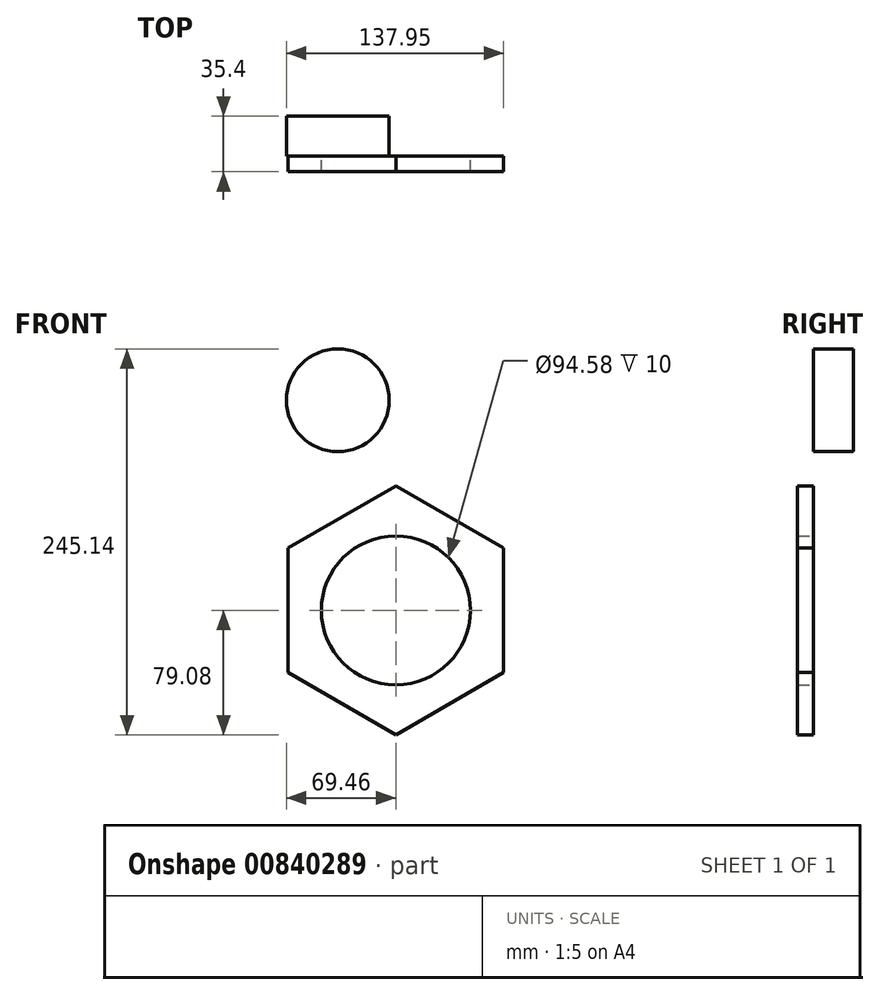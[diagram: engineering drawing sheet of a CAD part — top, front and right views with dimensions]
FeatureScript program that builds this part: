
annotation { "Feature Type Name" : "Feature", "Feature Type Description" : "" }
export const myFeature = defineFeature(function(context is Context, id is Id, definition is map)
    precondition{}
    {
        {
            var Q0;
            Q0=qCreatedBy(makeId("Front.planeOp"),FACE);
            var sketch = newSketch(context, id + "F0", { "sketchPlane" : qUnion([Q0])});
            skCircle(sketch, "E0.cCircle", {"center": v(0, 0) * mm, "radius": 79.08 * mm, "construction": true});
            skLineSegment(sketch, "E0.0", {"start": v(0, -79.08) * mm, "end": v(-68.49, -39.54) * mm});
            skLineSegment(sketch, "E0.1", {"start": v(-68.49, -39.54) * mm, "end": v(-68.49, 39.54) * mm});
            skLineSegment(sketch, "E0.2", {"start": v(-68.49, 39.54) * mm, "end": v(0, 79.08) * mm});
            skLineSegment(sketch, "E0.3", {"start": v(0, 79.08) * mm, "end": v(68.49, 39.54) * mm});
            skLineSegment(sketch, "E0.4", {"start": v(68.49, 39.54) * mm, "end": v(68.49, -39.54) * mm});
            skLineSegment(sketch, "E0.5", {"start": v(68.49, -39.54) * mm, "end": v(0, -79.08) * mm});
            skLineSegment(sketch, "E1.0", {"start": v(-2133.6, 3616.42) * mm, "end": v(-4198.71, 2424.13) * mm, "construction": true});
            skLineSegment(sketch, "E1.1", {"start": v(-4198.71, 2424.13) * mm, "end": v(-4198.71, 39.54) * mm, "construction": true});
            skCircle(sketch, "E2.0", {"center": v(0, 0) * mm, "radius": 4346.28 * mm, "construction": true});
            skSolve(sketch);
        }
        {
            var Q0;
            Q0=makeQuery(id+"F0.imprint","IMPRINT",FACE,{"disambiguationData":[TD([[makeQuery(id+"F0.imprint","IMPRINT",EDGE,{"derivedFrom":sQuery(id+"F0.wireOp",EDGE,"E0.0")}),-1.0]])]});
            var Q1;
            Q1=sQuery(id+"F0.wireOp",EDGE,"E0.0");
            var Q2;
            Q2=sQuery(id+"F0.wireOp",EDGE,"E0.2");
            var Q3;
            Q3=sQuery(id+"F0.wireOp",EDGE,"E0.4");
            var Q4;
            Q4=sQuery(id+"F0.wireOp",EDGE,"E0.3");
            var Q5;
            Q5=sQuery(id+"F0.wireOp",EDGE,"E0.1");
            extrude(context, id + "F1", {"entities" : qUnion([Q0]), "surfaceEntities" : qUnion([Q1, Q2, Q3, Q4, Q5]), "depth" : 10 * mm, "offsetDistance" : 25.4 * mm});
        }
        {
            var Q0;
            Q0=qCreatedBy(makeId("Front.planeOp"),FACE);
            var sketch = newSketch(context, id + "F2", { "sketchPlane" : qUnion([Q0])});
            skCircle(sketch, "E3", {"center": v(0, 0) * mm, "radius": 45.5 * mm});
            skSolve(sketch);
        }
        {
            var Q0;
            Q0 = qSketchRegion(id + "F2", true);
            extrude(context, id + "F3", {"entities" : qUnion([Q0]), "operationType" : NewBodyOperationType.REMOVE, "oppositeDirection" : true, "depth" : 25.4 * mm, "offsetDistance" : 25.4 * mm});
        }
        {
            var Q0;
            Q0=qCreatedBy(makeId("Front.planeOp"),FACE);
            var sketch = newSketch(context, id + "F4", { "sketchPlane" : qUnion([Q0])});
            skCircle(sketch, "E4", {"center": v(0, 0) * mm, "radius": 47.2 * mm});
            skSolve(sketch);
        }
        {
            var Q0;
            Q0 = qSketchRegion(id + "F4", true);
            extrude(context, id + "F5", {"entities" : qUnion([Q0]), "operationType" : NewBodyOperationType.REMOVE, "oppositeDirection" : true, "depth" : 25.4 * mm, "offsetDistance" : 25.4 * mm});
        }
        {
            var Q0;
            Q0=qCreatedBy(makeId("Front.planeOp"),FACE);
            var sketch = newSketch(context, id + "F6", { "sketchPlane" : qUnion([Q0])});
            skCircle(sketch, "E5", {"center": v(0, 0) * mm, "radius": 46.38 * mm});
            skSolve(sketch);
        }
        {
            var Q0;
            Q0 = qSketchRegion(id + "F6", true);
            extrude(context, id + "F7", {"entities" : qUnion([Q0]), "operationType" : NewBodyOperationType.REMOVE, "oppositeDirection" : true, "depth" : 10 * mm, "offsetDistance" : 25.4 * mm});
        }
        {
            var Q0;
            Q0=makeQuery(id+"F1.opExtrude","CAP_FACE",FACE,{"disambiguationData":[OSD([sQuery(id+"F0.wireOp",EDGE,"E0.0"),sQuery(id+"F0.wireOp",EDGE,"E0.1"),sQuery(id+"F0.wireOp",EDGE,"E0.2"),sQuery(id+"F0.wireOp",EDGE,"E0.3"),sQuery(id+"F0.wireOp",EDGE,"E0.4"),sQuery(id+"F0.wireOp",EDGE,"E0.5")])],"isStart":true});
            var sketch = newSketch(context, id + "F8", { "sketchPlane" : qUnion([Q0])});
            skCircle(sketch, "E6", {"center": v(0, 0) * mm, "radius": 47.3 * mm});
            skSolve(sketch);
        }
        {
            var Q0;
            Q0=makeQuery(id+"F8.imprint","IMPRINT",FACE,{"disambiguationData":[TD([[makeQuery(id+"F8.imprint","IMPRINT",EDGE,{"derivedFrom":sQuery(id+"F8.wireOp",EDGE,"E6")}),1.0]])]});
            extrude(context, id + "F9", {"entities" : qUnion([Q0]), "operationType" : NewBodyOperationType.REMOVE, "oppositeDirection" : true, "depth" : 25.4 * mm, "offsetDistance" : 25.4 * mm});
        }
        {
            var Q0;
            Q0=qCreatedBy(makeId("Front.planeOp"),FACE);
            var sketch = newSketch(context, id + "F10", { "sketchPlane" : qUnion([Q0])});
            skCircle(sketch, "E7", {"center": v(-36.85, 133.44) * mm, "radius": 26.27 * mm});
            skCircle(sketch, "E8.0", {"center": v(-36.85, 133.44) * mm, "radius": 32.62 * mm});
            skSolve(sketch);
        }
        {
            var Q0;
            Q0=makeQuery(id+"F10.imprint","IMPRINT",FACE,{"disambiguationData":[TD([[makeQuery(id+"F10.imprint","IMPRINT",EDGE,{"derivedFrom":sQuery(id+"F10.wireOp",EDGE,"E7")}),1.0]])]});
            var Q1;
            Q1=makeQuery(id+"F10.imprint","IMPRINT",FACE,{"disambiguationData":[TD([[makeQuery(id+"F10.imprint","IMPRINT",EDGE,{"derivedFrom":sQuery(id+"F10.wireOp",EDGE,"E7")}),-1.0]])]});
            extrude(context, id + "F11", {"entities" : qUnion([Q0, Q1]), "oppositeDirection" : true, "depth" : 25.4 * mm, "offsetDistance" : 25.4 * mm});
        }
    });
